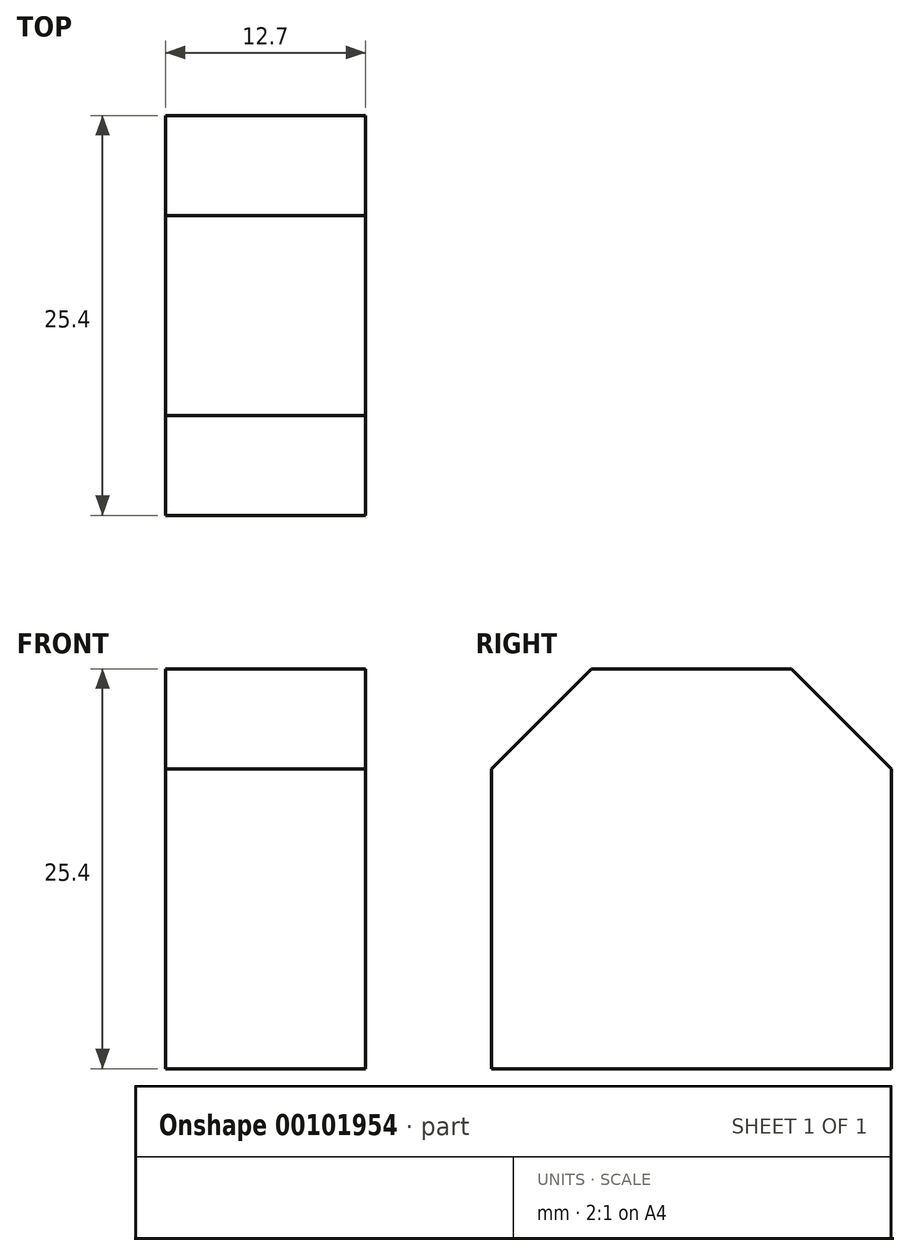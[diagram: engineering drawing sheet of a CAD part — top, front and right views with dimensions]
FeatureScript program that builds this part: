
annotation { "Feature Type Name" : "Feature", "Feature Type Description" : "" }
export const myFeature = defineFeature(function(context is Context, id is Id, definition is map)
    precondition{}
    {
        {
            var Q0;
            Q0=qCreatedBy(makeId("Right.planeOp"),FACE);
            var sketch = newSketch(context, id + "F0", { "sketchPlane" : qUnion([Q0])});
            skLineSegment(sketch, "E0", {"start": v(0, 0) * mm, "end": v(-25.4, 0) * mm});
            skLineSegment(sketch, "E1", {"start": v(-25.4, 0) * mm, "end": v(-25.4, 19.05) * mm});
            skLineSegment(sketch, "E2", {"start": v(-25.4, 19.05) * mm, "end": v(-19.05, 25.4) * mm});
            skLineSegment(sketch, "E3", {"start": v(-19.05, 25.4) * mm, "end": v(-6.35, 25.4) * mm});
            skLineSegment(sketch, "E4", {"start": v(-6.35, 25.4) * mm, "end": v(0, 19.05) * mm});
            skLineSegment(sketch, "E5", {"start": v(0, 19.05) * mm, "end": v(0, 0) * mm});
            skSolve(sketch);
        }
        {
            var Q0;
            Q0 = qSketchRegion(id + "F0", true);
            extrude(context, id + "F1", {"entities" : qUnion([Q0]), "depth" : 12.7 * mm});
        }
    });
